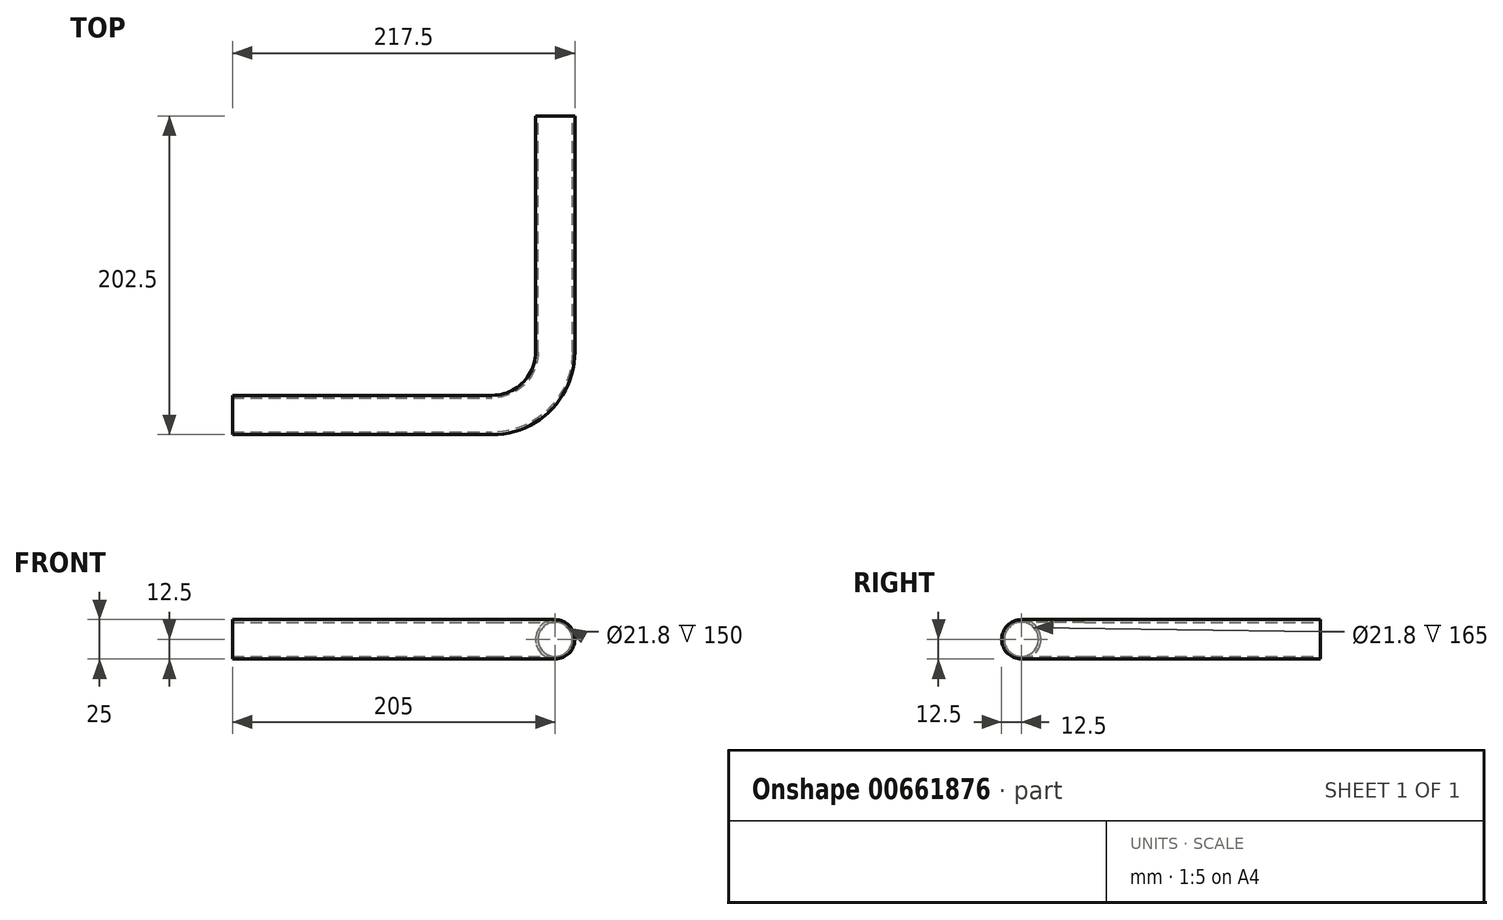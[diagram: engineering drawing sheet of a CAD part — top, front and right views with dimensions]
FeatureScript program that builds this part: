
annotation { "Feature Type Name" : "Feature", "Feature Type Description" : "" }
export const myFeature = defineFeature(function(context is Context, id is Id, definition is map)
    precondition{}
    {
        {
            var Q0;
            Q0=qCreatedBy(makeId("Top.planeOp"),FACE);
            var sketch = newSketch(context, id + "F0", { "sketchPlane" : qUnion([Q0])});
            skLineSegment(sketch, "E0", {"start": v(0, 0) * mm, "end": v(165, 0) * mm});
            skLineSegment(sketch, "E1", {"start": v(205, 40) * mm, "end": v(205, 190) * mm});
            skLineSegment(sketch, "E2", {"start": v(15, 0) * mm, "end": v(15, 180) * mm, "construction": true});
            skPoint(sketch, "E3.visualSharp", {"position": v(205, 0) * mm});
            skArc(sketch, "E3.filletArc", {"start": v(165, 0) * mm, "mid": v(193.28, 11.72) * mm, "end": v(205, 40) * mm});
            skPoint(sketch, "E4.visualSharp", {"position": v(205, 190) * mm});
            skSolve(sketch);
        }
        {
            var Q0;
            Q0=qCreatedBy(makeId("Right.planeOp"),FACE);
            var sketch = newSketch(context, id + "F1", { "sketchPlane" : qUnion([Q0])});
            skCircle(sketch, "E5", {"center": v(0, 0) * mm, "radius": 10.9 * mm});
            skCircle(sketch, "E6", {"center": v(0, 0) * mm, "radius": 12.5 * mm});
            skSolve(sketch);
        }
        {
            var Q0;
            Q0 = qSketchRegion(id + "F1", true);
            var Q1;
            Q1=sQuery(id+"F0.wireOp",EDGE,"E0");
            var Q2;
            Q2=sQuery(id+"F0.wireOp",EDGE,"E3.filletArc");
            var Q3;
            Q3=sQuery(id+"F0.wireOp",EDGE,"E1");
            var Q4;
            Q4=sQuery(id+"F0.wireOp",EDGE,"E4.filletArc");
            var Q5;
            Q5=sQuery(id+"F0.wireOp",EDGE,"Tx3sklj8-iBqD-HwL4-lU2J-3RWZXw7emWpM");
            sweep(context, id + "F2", {"profiles" : qUnion([Q0]), "path" : qUnion([Q1, Q2, Q3, Q4, Q5])});
        }
    });
